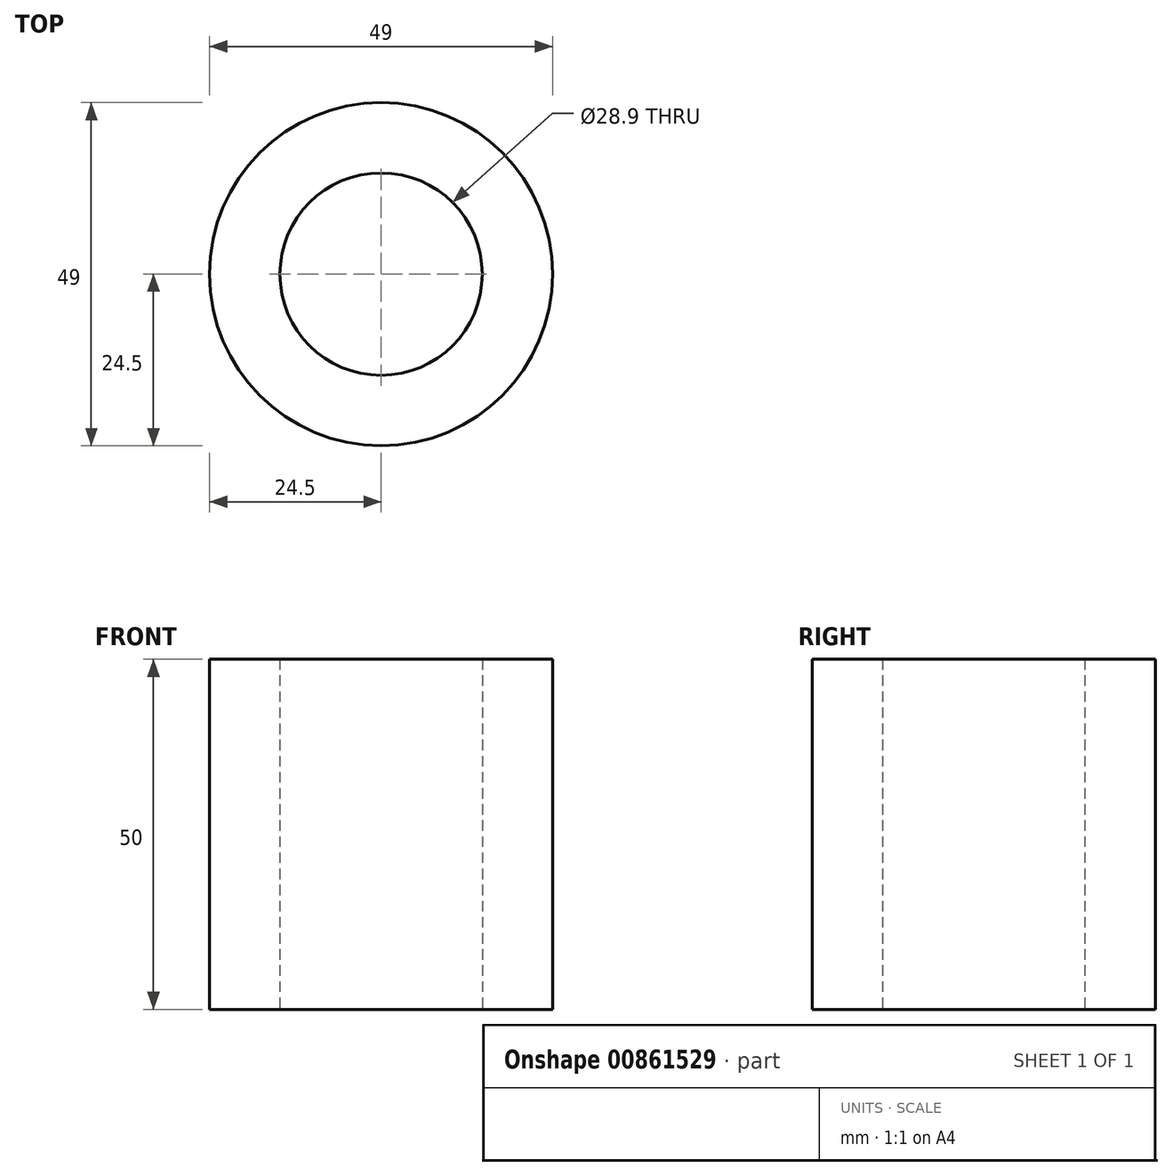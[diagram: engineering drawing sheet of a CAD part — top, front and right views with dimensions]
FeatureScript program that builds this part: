
annotation { "Feature Type Name" : "Feature", "Feature Type Description" : "" }
export const myFeature = defineFeature(function(context is Context, id is Id, definition is map)
    precondition{}
    {
        {
            var Q0;
            Q0=qCreatedBy(makeId("Top.planeOp"),FACE);
            var sketch = newSketch(context, id + "F0", { "sketchPlane" : qUnion([Q0])});
            skCircle(sketch, "E0", {"center": v(0, 0) * mm, "radius": 14.45 * mm});
            skCircle(sketch, "E1", {"center": v(0, 0) * mm, "radius": 24.5 * mm});
            skSolve(sketch);
        }
        {
            var Q0;
            Q0=makeQuery(id+"F0.imprint","IMPRINT",FACE,{"disambiguationData":[TD([[makeQuery(id+"F0.imprint","IMPRINT",EDGE,{"derivedFrom":sQuery(id+"F0.wireOp",EDGE,"E0")}),-1.0]])]});
            extrude(context, id + "F1", {"entities" : qUnion([Q0]), "depth" : 50 * mm, "offsetDistance" : 25 * mm});
        }
    });
